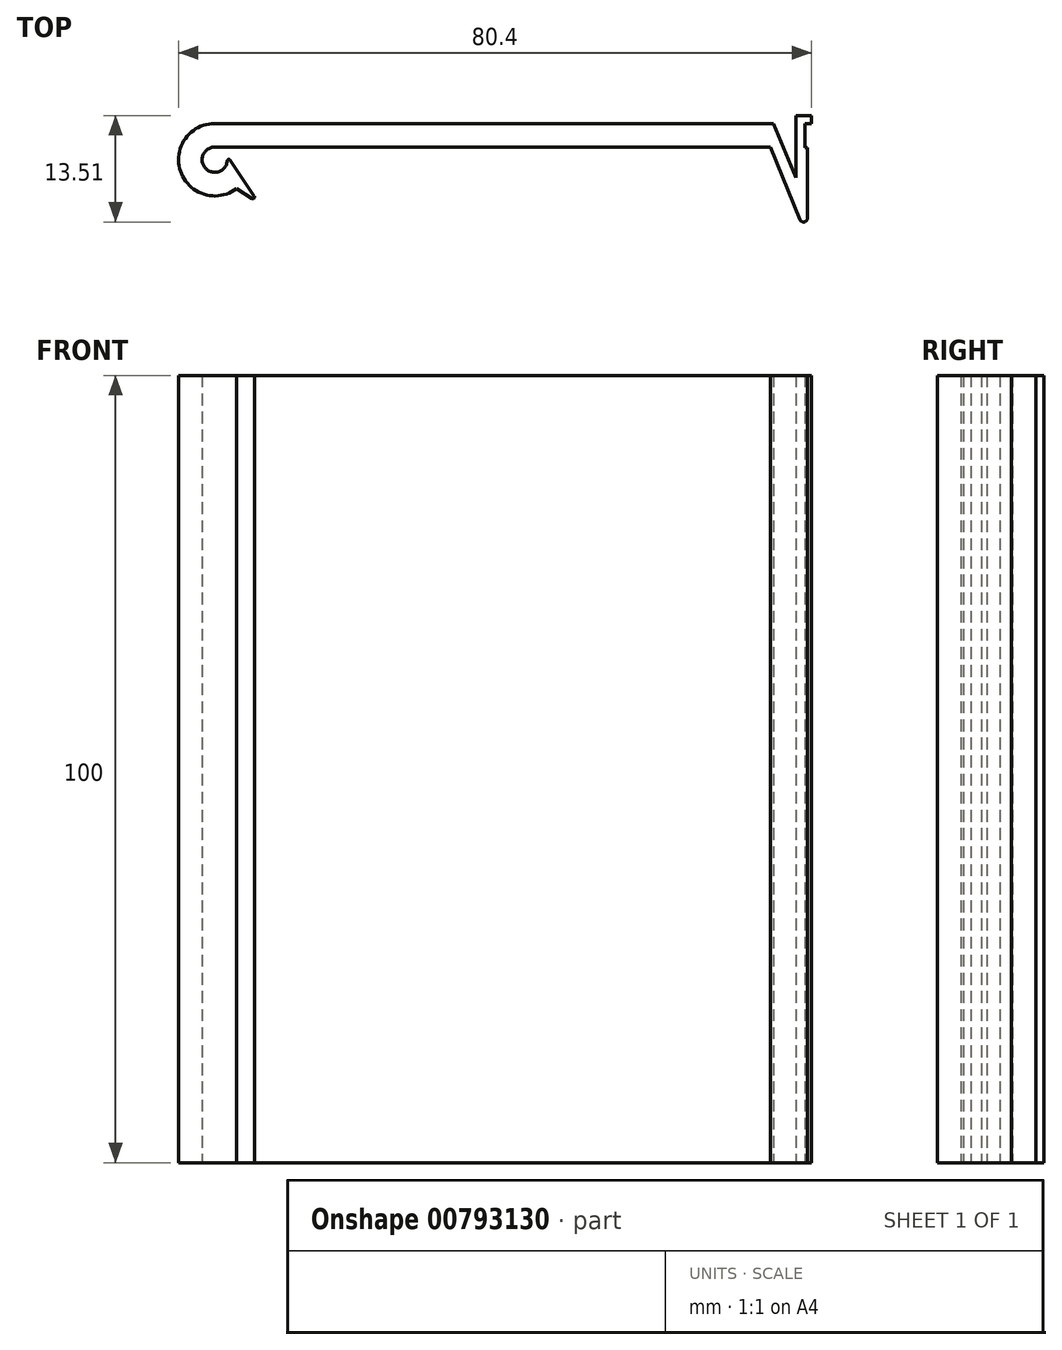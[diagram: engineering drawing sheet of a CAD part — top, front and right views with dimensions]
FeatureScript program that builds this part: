
annotation { "Feature Type Name" : "Feature", "Feature Type Description" : "" }
export const myFeature = defineFeature(function(context is Context, id is Id, definition is map)
    precondition{}
    {
        {
            var Q0;
            Q0=qCreatedBy(makeId("Top.planeOp"),FACE);
            var sketch = newSketch(context, id + "F0", { "sketchPlane" : qUnion([Q0])});
            skLineSegment(sketch, "E0", {"start": v(-0.09, 17.46) * mm, "end": v(-70.69, 17.46) * mm});
            skArc(sketch, "E1", {"start": v(-70.69, 17.46) * mm, "mid": v(-71.87, 14.79) * mm, "end": v(-69.1, 15.72) * mm});
            skLineSegment(sketch, "E2", {"start": v(-65.66, 11.23) * mm, "end": v(-68.73, 15.81) * mm});
            skLineSegment(sketch, "E3", {"start": v(-65.93, 10.95) * mm, "end": v(-67.91, 12.2) * mm});
            skArc(sketch, "E4", {"start": v(-70.69, 20.46) * mm, "mid": v(-75.05, 14.4) * mm, "end": v(-67.91, 12.2) * mm});
            skLineSegment(sketch, "E5", {"start": v(-0.09, 17.46) * mm, "end": v(3.65, 8.27) * mm});
            skLineSegment(sketch, "E6", {"start": v(-70.69, 20.46) * mm, "end": v(0.31, 20.46) * mm});
            skLineSegment(sketch, "E7", {"start": v(0.31, 20.46) * mm, "end": v(3.11, 13.57) * mm});
            skLineSegment(sketch, "E8", {"start": v(3.11, 13.57) * mm, "end": v(3.11, 21.46) * mm});
            skLineSegment(sketch, "E9", {"start": v(3.11, 21.46) * mm, "end": v(5.11, 21.46) * mm});
            skLineSegment(sketch, "E10", {"start": v(5.11, 21.46) * mm, "end": v(5.11, 20.46) * mm});
            skLineSegment(sketch, "E11", {"start": v(5.11, 20.46) * mm, "end": v(4.61, 20.46) * mm});
            skLineSegment(sketch, "E12", {"start": v(4.61, 17.36) * mm, "end": v(4.61, 8.45) * mm});
            skPoint(sketch, "E13.visualSharp", {"position": v(4.61, 5.9) * mm});
            skArc(sketch, "E13.filletArc", {"start": v(3.65, 8.27) * mm, "mid": v(4.21, 7.96) * mm, "end": v(4.61, 8.45) * mm});
            skLineSegment(sketch, "E14", {"start": v(4.61, 17.36) * mm, "end": v(4.31, 17.36) * mm});
            skLineSegment(sketch, "E15", {"start": v(4.31, 17.36) * mm, "end": v(4.31, 20.46) * mm});
            skLineSegment(sketch, "E16", {"start": v(4.31, 20.46) * mm, "end": v(4.61, 20.46) * mm});
            skPoint(sketch, "E17.visualSharp", {"position": v(-65.14, 10.45) * mm});
            skArc(sketch, "E17.filletArc", {"start": v(-65.93, 10.95) * mm, "mid": v(-65.68, 10.98) * mm, "end": v(-65.66, 11.23) * mm});
            skPoint(sketch, "E18.visualSharp", {"position": v(-69.36, 16.75) * mm});
            skArc(sketch, "E18.filletArc", {"start": v(-68.73, 15.81) * mm, "mid": v(-68.94, 15.9) * mm, "end": v(-69.1, 15.72) * mm});
            skSolve(sketch);
        }
        {
            var Q0;
            Q0=makeQuery(id+"F0.imprint","IMPRINT",FACE,{"disambiguationData":[TD([[makeQuery(id+"F0.imprint","IMPRINT",EDGE,{"derivedFrom":sQuery(id+"F0.wireOp",EDGE,"E0")}),-1.0]])]});
            extrude(context, id + "F1", {"entities" : qUnion([Q0]), "depth" : 100 * mm, "offsetDistance" : 25 * mm});
        }
    });
